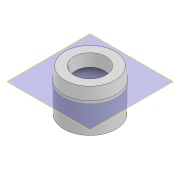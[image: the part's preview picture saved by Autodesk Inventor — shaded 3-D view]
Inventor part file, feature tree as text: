
AUTODESK INVENTOR PART (.ipt)
format: ipt  version: 2022 (Build 260153000, 153)  size: 105,472 bytes
history: native  units: mm
features: extrude x2, sketch x2, plane x1
ambient origin geometry x8: Origin, YZ Plane, XZ Plane, XY Plane, X Axis, Y Axis, Z Axis, Center Point
bodies: Volumenkörper1 (feature_tree)
feature tree (5):
  extrude  "Extrusion1"  Depth=7.6mm
  plane  "Arbeitsebene1"
  extrude  "Extrusion3"  Depth=8.0mm
  sketch  "Skizze1"  dims[d0=14.0mm d1=7.6mm]
  sketch  "Skizze3"  dims[d2=3.0mm d3=-1.396263mm d7=12.1mm d8=8.0mm d9=-0.174533mm]
